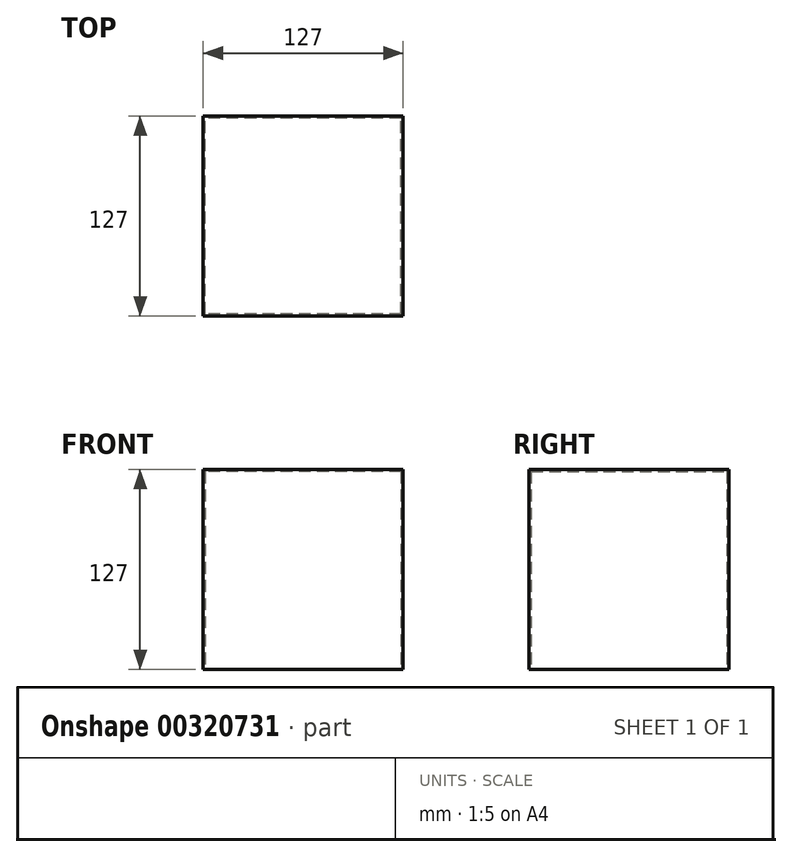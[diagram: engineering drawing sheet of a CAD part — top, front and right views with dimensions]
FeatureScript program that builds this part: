
annotation { "Feature Type Name" : "Feature", "Feature Type Description" : "" }
export const myFeature = defineFeature(function(context is Context, id is Id, definition is map)
    precondition{}
    {
        {
            var Q0;
            Q0=qCreatedBy(makeId("Front.planeOp"),FACE);
            var sketch = newSketch(context, id + "F0", { "sketchPlane" : qUnion([Q0])});
            skLineSegment(sketch, "E0.bottom", {"start": v(63.5, 63.5) * mm, "end": v(-63.5, 63.5) * mm});
            skLineSegment(sketch, "E0.top", {"start": v(63.5, -63.5) * mm, "end": v(-63.5, -63.5) * mm});
            skLineSegment(sketch, "E0.left", {"start": v(63.5, 63.5) * mm, "end": v(63.5, -63.5) * mm});
            skLineSegment(sketch, "E0.right", {"start": v(-63.5, 63.5) * mm, "end": v(-63.5, -63.5) * mm});
            skPoint(sketch, "E0.middle", {"position": v(0, 0) * mm});
            skSolve(sketch);
        }
        {
            var Q0;
            Q0=makeQuery(id+"F0.imprint","IMPRINT",FACE,{"disambiguationData":[TD([[makeQuery(id+"F0.imprint","IMPRINT",EDGE,{"derivedFrom":sQuery(id+"F0.wireOp",EDGE,"E0.bottom")}),1.0]])]});
            extrude(context, id + "F1", {"entities" : qUnion([Q0]), "depth" : 127 * mm, "symmetric" : true});
        }
        {
            var Q0;
            Q0=makeQuery(id+"F1.opExtrude","SWEPT_FACE",FACE,{"disambiguationData":[OSD([sQuery(id+"F0.wireOp",EDGE,"E0.top")])]});
            shell(context, id + "F2", {"entities" : qUnion([Q0]), "thickness" : 1.27 * mm});
        }
    });
